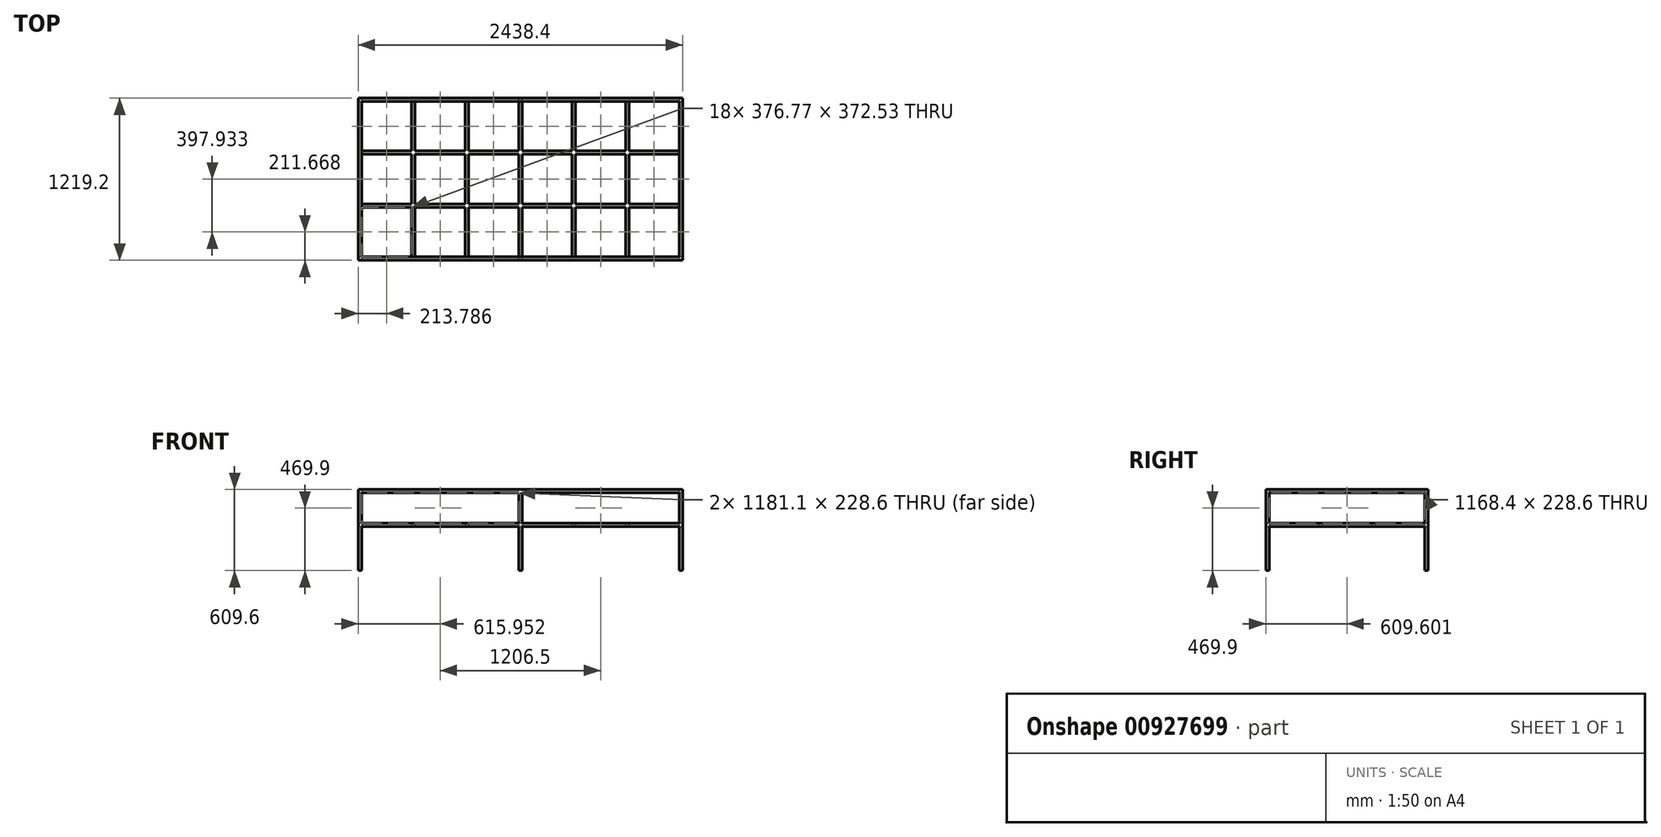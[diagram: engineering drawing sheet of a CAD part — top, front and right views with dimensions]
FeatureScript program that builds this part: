
annotation { "Feature Type Name" : "Feature", "Feature Type Description" : "" }
export const myFeature = defineFeature(function(context is Context, id is Id, definition is map)
    precondition{}
    {
        {
            var Q0;
            Q0=qCreatedBy(makeId("Top.planeOp"),FACE);
            var sketch = newSketch(context, id + "F0", { "sketchPlane" : qUnion([Q0])});
            skLineSegment(sketch, "E0.bottom", {"start": v(-287.49, 1104.34) * mm, "end": v(2150.91, 1104.34) * mm});
            skLineSegment(sketch, "E0.top", {"start": v(-287.49, -114.86) * mm, "end": v(2150.91, -114.86) * mm});
            skLineSegment(sketch, "E0.left", {"start": v(-287.49, 1104.34) * mm, "end": v(-287.49, -114.86) * mm});
            skLineSegment(sketch, "E0.right", {"start": v(2150.91, 1104.34) * mm, "end": v(2150.91, -114.86) * mm});
            skLineSegment(sketch, "E1.bottom", {"start": v(2150.91, 1078.94) * mm, "end": v(1748.75, 1078.94) * mm});
            skLineSegment(sketch, "E1.top", {"start": v(2150.91, 1104.34) * mm, "end": v(-287.49, 1104.34) * mm});
            skLineSegment(sketch, "E1.left", {"start": v(2150.91, 1078.94) * mm, "end": v(2150.91, 1104.34) * mm});
            skLineSegment(sketch, "E1.right", {"start": v(-287.49, 1078.94) * mm, "end": v(-287.49, 1104.34) * mm});
            skLineSegment(sketch, "E2.bottom", {"start": v(-287.49, 1104.34) * mm, "end": v(-262.09, 1104.34) * mm});
            skLineSegment(sketch, "E2.top", {"start": v(-287.49, -114.86) * mm, "end": v(-262.09, -114.86) * mm});
            skLineSegment(sketch, "E2.right", {"start": v(-262.09, 1104.34) * mm, "end": v(-262.09, 706.4) * mm});
            skLineSegment(sketch, "E3.top", {"start": v(-287.49, -89.46) * mm, "end": v(114.68, -89.46) * mm});
            skLineSegment(sketch, "E3.left", {"start": v(-287.49, -114.86) * mm, "end": v(-287.49, -89.46) * mm});
            skLineSegment(sketch, "E3.right", {"start": v(2150.91, -114.86) * mm, "end": v(2150.91, -89.46) * mm});
            skLineSegment(sketch, "E4.bottom", {"start": v(2150.91, -114.86) * mm, "end": v(2125.51, -114.86) * mm});
            skLineSegment(sketch, "E4.top", {"start": v(2150.91, 1104.34) * mm, "end": v(2125.51, 1104.34) * mm});
            skLineSegment(sketch, "E4.left", {"start": v(2150.91, -114.86) * mm, "end": v(2150.91, 1104.34) * mm});
            skLineSegment(sketch, "E4.right", {"start": v(2125.51, -114.86) * mm, "end": v(2125.51, 283.07) * mm});
            skLineSegment(sketch, "E5.bottom", {"start": v(919.01, 1104.34) * mm, "end": v(944.41, 1104.34) * mm});
            skLineSegment(sketch, "E5.top", {"start": v(919.01, -114.86) * mm, "end": v(944.41, -114.86) * mm});
            skLineSegment(sketch, "E5.left", {"start": v(919.01, 1104.34) * mm, "end": v(919.01, 706.4) * mm});
            skLineSegment(sketch, "E5.right", {"start": v(944.41, 1104.34) * mm, "end": v(944.41, 706.4) * mm});
            skLineSegment(sketch, "E6.left", {"start": v(114.68, 1078.94) * mm, "end": v(114.68, 706.4) * mm});
            skLineSegment(sketch, "E6.right", {"start": v(140.08, 1078.94) * mm, "end": v(140.08, 706.4) * mm});
            skLineSegment(sketch, "E7.left", {"start": v(516.85, 1078.94) * mm, "end": v(516.85, 706.4) * mm});
            skLineSegment(sketch, "E7.right", {"start": v(542.25, 1078.94) * mm, "end": v(542.25, 706.4) * mm});
            skLineSegment(sketch, "E8.left", {"start": v(1321.18, 1078.94) * mm, "end": v(1321.18, 706.4) * mm});
            skLineSegment(sketch, "E8.right", {"start": v(1346.58, 1078.94) * mm, "end": v(1346.58, 706.4) * mm});
            skLineSegment(sketch, "E9.left", {"start": v(1723.35, 1078.94) * mm, "end": v(1723.35, 706.4) * mm});
            skLineSegment(sketch, "E9.right", {"start": v(1748.75, 1078.94) * mm, "end": v(1748.75, 706.4) * mm});
            skLineSegment(sketch, "E10.bottom", {"start": v(-262.09, 706.4) * mm, "end": v(114.68, 706.4) * mm});
            skLineSegment(sketch, "E10.top", {"start": v(-262.09, 681) * mm, "end": v(114.68, 681) * mm});
            skLineSegment(sketch, "E10.right", {"start": v(2125.51, 706.4) * mm, "end": v(2125.51, 681) * mm});
            skLineSegment(sketch, "E11.bottom", {"start": v(-262.09, 308.47) * mm, "end": v(114.68, 308.47) * mm});
            skLineSegment(sketch, "E11.top", {"start": v(-262.09, 283.07) * mm, "end": v(114.68, 283.07) * mm});
            skLineSegment(sketch, "E12.trimOffspring", {"start": v(140.08, 706.4) * mm, "end": v(516.85, 706.4) * mm});
            skLineSegment(sketch, "E13.trimOffspring", {"start": v(114.68, 681) * mm, "end": v(114.68, 308.47) * mm});
            skLineSegment(sketch, "E14.trimOffspring", {"start": v(140.08, 681) * mm, "end": v(140.08, 308.47) * mm});
            skLineSegment(sketch, "E15.trimOffspring", {"start": v(140.08, 681) * mm, "end": v(516.85, 681) * mm});
            skLineSegment(sketch, "E16.trimOffspring", {"start": v(140.08, 308.47) * mm, "end": v(516.85, 308.47) * mm});
            skLineSegment(sketch, "E17.trimOffspring", {"start": v(114.68, 283.07) * mm, "end": v(114.68, -89.46) * mm});
            skLineSegment(sketch, "E18.trimOffspring", {"start": v(140.08, 283.07) * mm, "end": v(516.85, 283.07) * mm});
            skLineSegment(sketch, "E19.trimOffspring", {"start": v(140.08, 283.07) * mm, "end": v(140.08, -89.46) * mm});
            skLineSegment(sketch, "E20.trimOffspring", {"start": v(516.85, 283.07) * mm, "end": v(516.85, -89.46) * mm});
            skLineSegment(sketch, "E21.trimOffspring", {"start": v(542.25, 283.07) * mm, "end": v(542.25, -89.46) * mm});
            skLineSegment(sketch, "E22.trimOffspring", {"start": v(542.25, 308.47) * mm, "end": v(919.01, 308.47) * mm});
            skLineSegment(sketch, "E23.trimOffspring", {"start": v(542.25, 283.07) * mm, "end": v(919.01, 283.07) * mm});
            skLineSegment(sketch, "E24.trimOffspring", {"start": v(944.41, 308.47) * mm, "end": v(1321.18, 308.47) * mm});
            skLineSegment(sketch, "E25.trimOffspring", {"start": v(919.01, 283.07) * mm, "end": v(919.01, -114.86) * mm});
            skLineSegment(sketch, "E26.trimOffspring", {"start": v(944.41, 283.07) * mm, "end": v(944.41, -114.86) * mm});
            skLineSegment(sketch, "E27.trimOffspring", {"start": v(944.41, 283.07) * mm, "end": v(1321.18, 283.07) * mm});
            skLineSegment(sketch, "E28.trimOffspring", {"start": v(1321.18, 283.07) * mm, "end": v(1321.18, -89.46) * mm});
            skLineSegment(sketch, "E29.trimOffspring", {"start": v(1346.58, 308.47) * mm, "end": v(1723.35, 308.47) * mm});
            skLineSegment(sketch, "E30.trimOffspring", {"start": v(1346.58, 283.07) * mm, "end": v(1346.58, -89.46) * mm});
            skLineSegment(sketch, "E31.trimOffspring", {"start": v(1346.58, 283.07) * mm, "end": v(1723.35, 283.07) * mm});
            skLineSegment(sketch, "E32.trimOffspring", {"start": v(1748.75, 308.47) * mm, "end": v(2125.51, 308.47) * mm});
            skLineSegment(sketch, "E33.trimOffspring", {"start": v(1723.35, 283.07) * mm, "end": v(1723.35, -89.46) * mm});
            skLineSegment(sketch, "E34.trimOffspring", {"start": v(1748.75, 283.07) * mm, "end": v(2125.51, 283.07) * mm});
            skLineSegment(sketch, "E35.trimOffspring", {"start": v(1748.75, 283.07) * mm, "end": v(1748.75, -89.46) * mm});
            skLineSegment(sketch, "E36.trimOffspring", {"start": v(2125.51, 308.47) * mm, "end": v(2125.51, 1104.34) * mm});
            skLineSegment(sketch, "E37.trimOffspring", {"start": v(1748.75, -89.46) * mm, "end": v(2150.91, -89.46) * mm});
            skLineSegment(sketch, "E38.trimOffspring", {"start": v(1346.58, -89.46) * mm, "end": v(1723.35, -89.46) * mm});
            skLineSegment(sketch, "E39.trimOffspring", {"start": v(542.25, -89.46) * mm, "end": v(1321.18, -89.46) * mm});
            skLineSegment(sketch, "E40.trimOffspring", {"start": v(140.08, -89.46) * mm, "end": v(516.85, -89.46) * mm});
            skLineSegment(sketch, "E41.trimOffspring", {"start": v(-262.09, 283.07) * mm, "end": v(-262.09, -114.86) * mm});
            skLineSegment(sketch, "E42.trimOffspring", {"start": v(-262.09, 681) * mm, "end": v(-262.09, 308.47) * mm});
            skLineSegment(sketch, "E43.trimOffspring", {"start": v(114.68, 1078.94) * mm, "end": v(-287.49, 1078.94) * mm});
            skLineSegment(sketch, "E44.trimOffspring", {"start": v(516.85, 1078.94) * mm, "end": v(140.08, 1078.94) * mm});
            skLineSegment(sketch, "E45.trimOffspring", {"start": v(1321.18, 1078.94) * mm, "end": v(542.25, 1078.94) * mm});
            skLineSegment(sketch, "E46.trimOffspring", {"start": v(1723.35, 1078.94) * mm, "end": v(1346.58, 1078.94) * mm});
            skLineSegment(sketch, "E47.trimOffspring", {"start": v(516.85, 681) * mm, "end": v(516.85, 308.47) * mm});
            skLineSegment(sketch, "E48.trimOffspring", {"start": v(542.25, 681) * mm, "end": v(542.25, 308.47) * mm});
            skLineSegment(sketch, "E49.trimOffspring", {"start": v(542.25, 706.4) * mm, "end": v(919.01, 706.4) * mm});
            skLineSegment(sketch, "E50.trimOffspring", {"start": v(542.25, 681) * mm, "end": v(919.01, 681) * mm});
            skLineSegment(sketch, "E51.trimOffspring", {"start": v(944.41, 706.4) * mm, "end": v(1321.18, 706.4) * mm});
            skLineSegment(sketch, "E52.trimOffspring", {"start": v(944.41, 681) * mm, "end": v(1321.18, 681) * mm});
            skLineSegment(sketch, "E53.trimOffspring", {"start": v(919.01, 681) * mm, "end": v(919.01, 308.47) * mm});
            skLineSegment(sketch, "E54.trimOffspring", {"start": v(944.41, 681) * mm, "end": v(944.41, 308.47) * mm});
            skLineSegment(sketch, "E55.trimOffspring", {"start": v(1321.18, 681) * mm, "end": v(1321.18, 308.47) * mm});
            skLineSegment(sketch, "E56.trimOffspring", {"start": v(1346.58, 681) * mm, "end": v(1346.58, 308.47) * mm});
            skLineSegment(sketch, "E57.trimOffspring", {"start": v(1346.58, 706.4) * mm, "end": v(1723.35, 706.4) * mm});
            skLineSegment(sketch, "E58.trimOffspring", {"start": v(1346.58, 681) * mm, "end": v(1723.35, 681) * mm});
            skLineSegment(sketch, "E59.trimOffspring", {"start": v(1748.75, 681) * mm, "end": v(1748.75, 308.47) * mm});
            skLineSegment(sketch, "E60.trimOffspring", {"start": v(1748.75, 706.4) * mm, "end": v(2125.51, 706.4) * mm});
            skLineSegment(sketch, "E61.trimOffspring", {"start": v(1723.35, 681) * mm, "end": v(1723.35, 308.47) * mm});
            skLineSegment(sketch, "E62.trimOffspring", {"start": v(1748.75, 681) * mm, "end": v(2125.51, 681) * mm});
            skSolve(sketch);
        }
        {
            var Q0;
            {var subQ0=sQuery(id+"F0.wireOp",EDGE,"E0.right");var subQ1=sQuery(id+"F0.wireOp",EDGE,"E0.bottom");var subQ2=makeQuery(id+"F0.imprint","INTERSECT",VERTEX,{"derivedFrom":[subQ1,subQ0]});var subQ10=sQuery(id+"F0.wireOp",EDGE,"E0.top");var subQ11=makeQuery(id+"F0.imprint","INTERSECT",VERTEX,{"derivedFrom":[subQ10,subQ0]});var subQ19=sQuery(id+"F0.wireOp",EDGE,"E0.left");var subQ20=makeQuery(id+"F0.imprint","INTERSECT",VERTEX,{"derivedFrom":[subQ1,subQ19]});var subQ28=sQuery(id+"F0.wireOp",EDGE,"E5.right");var subQ29=makeQuery(id+"F0.imprint","INTERSECT",VERTEX,{"derivedFrom":[subQ1,subQ28]});var subQ38=sQuery(id+"F0.wireOp",EDGE,"E41.trimOffspring");var subQ39=makeQuery(id+"F0.imprint","INTERSECT",VERTEX,{"derivedFrom":[subQ10,subQ38]});var subQ47=sQuery(id+"F0.wireOp",EDGE,"E26.trimOffspring");var subQ61=makeQuery(id+"F0.imprint","INTERSECT",VERTEX,{"derivedFrom":[subQ10,subQ47]});var subQ62=sQuery(id+"F0.wireOp",EDGE,"E6.left");Q0=qUnion([makeQuery(id+"F0.imprint","IMPRINT",FACE,{"disambiguationData":[TD([[makeQuery(id+"F0.imprint","IMPRINT",EDGE,{"disambiguationData":[TD([[subQ61,1.0]])],"derivedFrom":subQ10}),1.0]])]}),makeQuery(id+"F0.imprint","IMPRINT",FACE,{"disambiguationData":[TD([[makeQuery(id+"F0.imprint","IMPRINT",EDGE,{"derivedFrom":subQ62}),1.0]])]}),makeQuery(id+"F0.imprint","IMPRINT",FACE,{"disambiguationData":[TD([[makeQuery(id+"F0.imprint","IMPRINT",EDGE,{"disambiguationData":[TD([[subQ39,1.0]])],"derivedFrom":subQ10}),1.0]])]}),makeQuery(id+"F0.imprint","IMPRINT",FACE,{"disambiguationData":[TD([[makeQuery(id+"F0.imprint","IMPRINT",EDGE,{"disambiguationData":[TD([[subQ29,1.0]])],"derivedFrom":subQ1}),-1.0]])]}),makeQuery(id+"F0.imprint","IMPRINT",FACE,{"disambiguationData":[TD([[makeQuery(id+"F0.imprint","IMPRINT",EDGE,{"disambiguationData":[TD([[subQ20,-1.0]])],"derivedFrom":subQ1}),-1.0]])]}),makeQuery(id+"F0.imprint","IMPRINT",FACE,{"disambiguationData":[TD([[makeQuery(id+"F0.imprint","IMPRINT",EDGE,{"disambiguationData":[TD([[subQ11,1.0]])],"derivedFrom":subQ10}),1.0]])]}),makeQuery(id+"F0.imprint","IMPRINT",FACE,{"disambiguationData":[TD([[makeQuery(id+"F0.imprint","IMPRINT",EDGE,{"disambiguationData":[TD([[subQ2,1.0]])],"derivedFrom":subQ1}),-1.0]])]})]);}
            extrude(context, id + "F1", {"entities" : qUnion([Q0]), "depth" : 25.4 * mm, "offsetDistance" : 25.4 * mm});
        }
        {
            var Q0;
            {var subQ0=sQuery(id+"F0.wireOp",EDGE,"E0.left");var subQ1=sQuery(id+"F0.wireOp",EDGE,"E0.bottom");var subQ2=makeQuery(id+"F0.imprint","INTERSECT",VERTEX,{"derivedFrom":[subQ1,subQ0]});Q0=makeQuery(id+"F0.imprint","IMPRINT",FACE,{"disambiguationData":[TD([[makeQuery(id+"F0.imprint","IMPRINT",EDGE,{"disambiguationData":[TD([[subQ2,-1.0]])],"derivedFrom":subQ1}),-1.0]])]});}
            var Q1;
            {var subQ0=sQuery(id+"F0.wireOp",EDGE,"E41.trimOffspring");var subQ1=sQuery(id+"F0.wireOp",EDGE,"E0.top");var subQ2=makeQuery(id+"F0.imprint","INTERSECT",VERTEX,{"derivedFrom":[subQ1,subQ0]});Q1=makeQuery(id+"F0.imprint","IMPRINT",FACE,{"disambiguationData":[TD([[makeQuery(id+"F0.imprint","IMPRINT",EDGE,{"disambiguationData":[TD([[subQ2,1.0]])],"derivedFrom":subQ1}),1.0]])]});}
            var Q2;
            {var subQ0=sQuery(id+"F0.wireOp",EDGE,"E26.trimOffspring");var subQ1=sQuery(id+"F0.wireOp",EDGE,"E0.top");var subQ2=makeQuery(id+"F0.imprint","INTERSECT",VERTEX,{"derivedFrom":[subQ1,subQ0]});Q2=makeQuery(id+"F0.imprint","IMPRINT",FACE,{"disambiguationData":[TD([[makeQuery(id+"F0.imprint","IMPRINT",EDGE,{"disambiguationData":[TD([[subQ2,1.0]])],"derivedFrom":subQ1}),1.0]])]});}
            var Q3;
            {var subQ0=sQuery(id+"F0.wireOp",EDGE,"E0.right");var subQ1=sQuery(id+"F0.wireOp",EDGE,"E0.top");var subQ2=makeQuery(id+"F0.imprint","INTERSECT",VERTEX,{"derivedFrom":[subQ1,subQ0]});Q3=makeQuery(id+"F0.imprint","IMPRINT",FACE,{"disambiguationData":[TD([[makeQuery(id+"F0.imprint","IMPRINT",EDGE,{"disambiguationData":[TD([[subQ2,1.0]])],"derivedFrom":subQ1}),1.0]])]});}
            var Q4;
            {var subQ0=sQuery(id+"F0.wireOp",EDGE,"E0.right");var subQ1=sQuery(id+"F0.wireOp",EDGE,"E0.bottom");var subQ2=makeQuery(id+"F0.imprint","INTERSECT",VERTEX,{"derivedFrom":[subQ1,subQ0]});Q4=makeQuery(id+"F0.imprint","IMPRINT",FACE,{"disambiguationData":[TD([[makeQuery(id+"F0.imprint","IMPRINT",EDGE,{"disambiguationData":[TD([[subQ2,1.0]])],"derivedFrom":subQ1}),-1.0]])]});}
            var Q5;
            {var subQ0=sQuery(id+"F0.wireOp",EDGE,"E5.right");var subQ1=sQuery(id+"F0.wireOp",EDGE,"E0.bottom");var subQ2=makeQuery(id+"F0.imprint","INTERSECT",VERTEX,{"derivedFrom":[subQ1,subQ0]});Q5=makeQuery(id+"F0.imprint","IMPRINT",FACE,{"disambiguationData":[TD([[makeQuery(id+"F0.imprint","IMPRINT",EDGE,{"disambiguationData":[TD([[subQ2,1.0]])],"derivedFrom":subQ1}),-1.0]])]});}
            extrude(context, id + "F2", {"entities" : qUnion([Q0, Q1, Q2, Q3, Q4, Q5]), "operationType" : NewBodyOperationType.ADD, "oppositeDirection" : true, "depth" : 330.2 * mm, "offsetDistance" : 25.4 * mm});
        }
        {
            var Q0;
            {var subQ0=sQuery(id+"F0.wireOp",EDGE,"E0.left");var subQ1=sQuery(id+"F0.wireOp",EDGE,"E0.bottom");var subQ2=makeQuery(id+"F0.imprint","INTERSECT",VERTEX,{"derivedFrom":[subQ1,subQ0]});Q0=makeQuery(id+"F0.imprint","IMPRINT",FACE,{"disambiguationData":[TD([[makeQuery(id+"F0.imprint","IMPRINT",EDGE,{"disambiguationData":[TD([[subQ2,-1.0]])],"derivedFrom":subQ1}),-1.0]])]});}
            var Q1;
            {var subQ0=sQuery(id+"F0.wireOp",EDGE,"E5.right");var subQ1=sQuery(id+"F0.wireOp",EDGE,"E0.bottom");var subQ2=makeQuery(id+"F0.imprint","INTERSECT",VERTEX,{"derivedFrom":[subQ1,subQ0]});Q1=makeQuery(id+"F0.imprint","IMPRINT",FACE,{"disambiguationData":[TD([[makeQuery(id+"F0.imprint","IMPRINT",EDGE,{"disambiguationData":[TD([[subQ2,1.0]])],"derivedFrom":subQ1}),-1.0]])]});}
            var Q2;
            {var subQ0=sQuery(id+"F0.wireOp",EDGE,"E41.trimOffspring");var subQ1=sQuery(id+"F0.wireOp",EDGE,"E0.top");var subQ2=makeQuery(id+"F0.imprint","INTERSECT",VERTEX,{"derivedFrom":[subQ1,subQ0]});Q2=makeQuery(id+"F0.imprint","IMPRINT",FACE,{"disambiguationData":[TD([[makeQuery(id+"F0.imprint","IMPRINT",EDGE,{"disambiguationData":[TD([[subQ2,1.0]])],"derivedFrom":subQ1}),1.0]])]});}
            var Q3;
            {var subQ0=sQuery(id+"F0.wireOp",EDGE,"E26.trimOffspring");var subQ1=sQuery(id+"F0.wireOp",EDGE,"E0.top");var subQ2=makeQuery(id+"F0.imprint","INTERSECT",VERTEX,{"derivedFrom":[subQ1,subQ0]});Q3=makeQuery(id+"F0.imprint","IMPRINT",FACE,{"disambiguationData":[TD([[makeQuery(id+"F0.imprint","IMPRINT",EDGE,{"disambiguationData":[TD([[subQ2,1.0]])],"derivedFrom":subQ1}),1.0]])]});}
            var Q4;
            {var subQ0=sQuery(id+"F0.wireOp",EDGE,"E0.right");var subQ1=sQuery(id+"F0.wireOp",EDGE,"E0.top");var subQ2=makeQuery(id+"F0.imprint","INTERSECT",VERTEX,{"derivedFrom":[subQ1,subQ0]});Q4=makeQuery(id+"F0.imprint","IMPRINT",FACE,{"disambiguationData":[TD([[makeQuery(id+"F0.imprint","IMPRINT",EDGE,{"disambiguationData":[TD([[subQ2,1.0]])],"derivedFrom":subQ1}),1.0]])]});}
            var Q5;
            {var subQ0=sQuery(id+"F0.wireOp",EDGE,"E0.right");var subQ1=sQuery(id+"F0.wireOp",EDGE,"E0.bottom");var subQ2=makeQuery(id+"F0.imprint","INTERSECT",VERTEX,{"derivedFrom":[subQ1,subQ0]});Q5=makeQuery(id+"F0.imprint","IMPRINT",FACE,{"disambiguationData":[TD([[makeQuery(id+"F0.imprint","IMPRINT",EDGE,{"disambiguationData":[TD([[subQ2,1.0]])],"derivedFrom":subQ1}),-1.0]])]});}
            extrude(context, id + "F3", {"entities" : qUnion([Q0, Q1, Q2, Q3, Q4, Q5]), "operationType" : NewBodyOperationType.ADD, "depth" : 254 * mm, "offsetDistance" : 25.4 * mm});
        }
        {
            var Q0;
            Q0=makeQuery(id+"F3.opExtrude","CAP_FACE",FACE,{"disambiguationData":[OSD([sQuery(id+"F0.wireOp",EDGE,"E0.top"),sQuery(id+"F0.wireOp",EDGE,"E0.left"),sQuery(id+"F0.wireOp",EDGE,"E3.top"),sQuery(id+"F0.wireOp",EDGE,"E41.trimOffspring")])],"isStart":false});
            var sketch = newSketch(context, id + "F4", { "sketchPlane" : qUnion([Q0])});
            skLineSegment(sketch, "E63.bottom", {"start": v(-287.49, -114.86) * mm, "end": v(2150.91, -114.86) * mm});
            skLineSegment(sketch, "E63.top", {"start": v(-287.49, 1104.34) * mm, "end": v(2150.91, 1104.34) * mm});
            skLineSegment(sketch, "E63.left", {"start": v(-287.49, -114.86) * mm, "end": v(-287.49, 1104.34) * mm});
            skLineSegment(sketch, "E63.right", {"start": v(2150.91, -114.86) * mm, "end": v(2150.91, 1104.34) * mm});
            skLineSegment(sketch, "E64.bottom", {"start": v(-262.09, -89.46) * mm, "end": v(2125.51, -89.46) * mm});
            skLineSegment(sketch, "E64.top", {"start": v(-262.09, 1078.94) * mm, "end": v(2125.51, 1078.94) * mm});
            skLineSegment(sketch, "E64.left", {"start": v(-262.09, -89.46) * mm, "end": v(-262.09, 1078.94) * mm});
            skLineSegment(sketch, "E64.right", {"start": v(2125.51, -89.46) * mm, "end": v(2125.51, 1078.94) * mm});
            skSolve(sketch);
        }
        {
            var Q0;
            Q0 = qSketchRegion(id + "F4", true);
            extrude(context, id + "F5", {"entities" : qUnion([Q0]), "operationType" : NewBodyOperationType.ADD, "depth" : 25.4 * mm, "offsetDistance" : 25.4 * mm});
        }
    });
